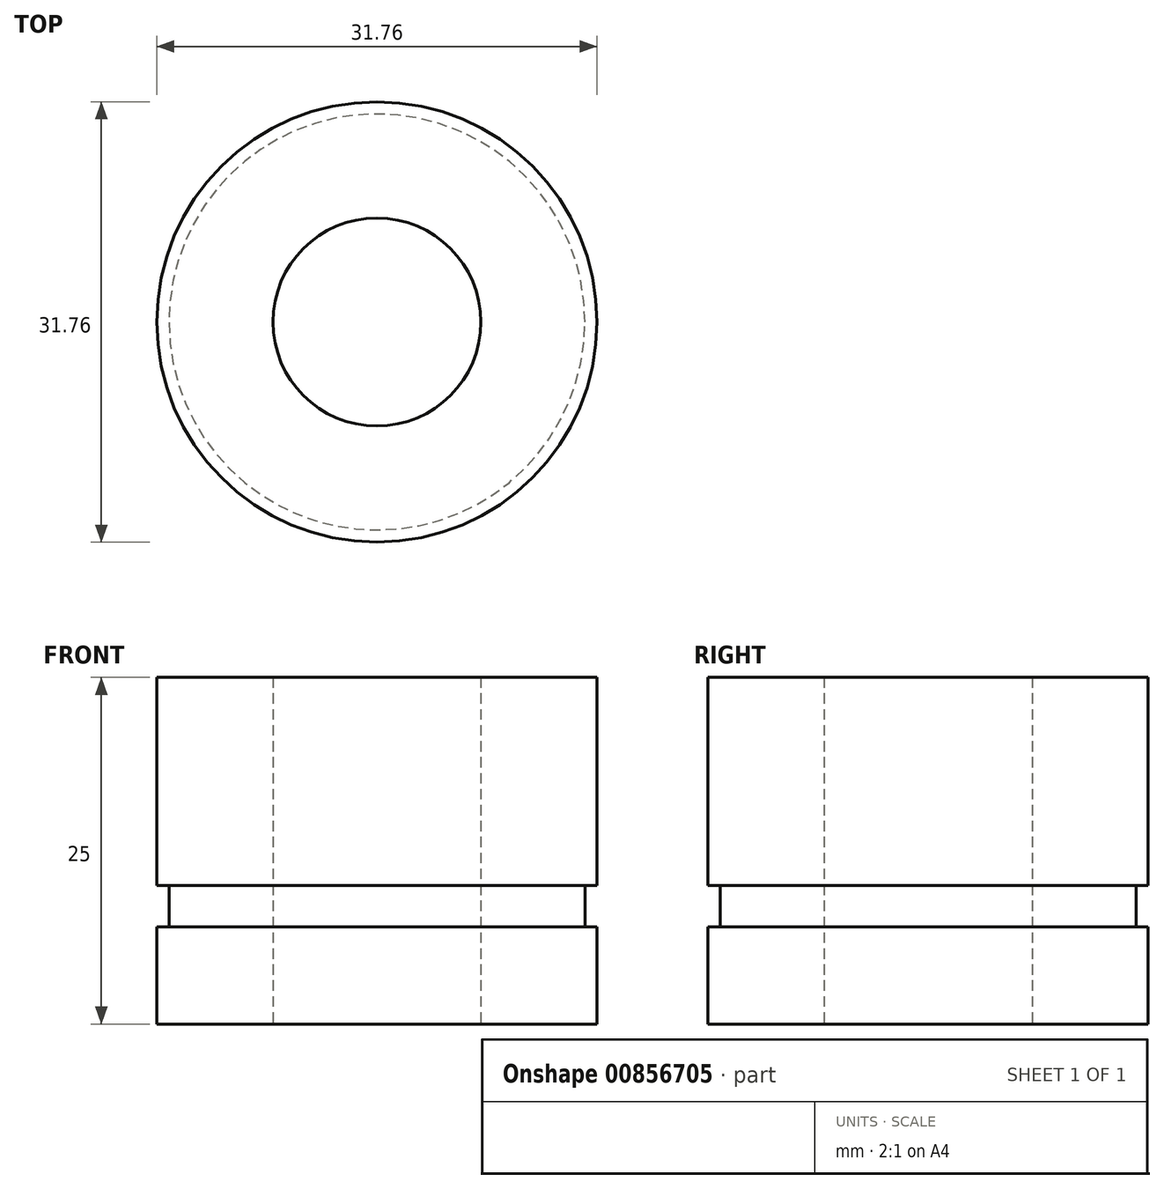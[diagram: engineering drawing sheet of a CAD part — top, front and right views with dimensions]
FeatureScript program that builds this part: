
annotation { "Feature Type Name" : "Feature", "Feature Type Description" : "" }
export const myFeature = defineFeature(function(context is Context, id is Id, definition is map)
    precondition{}
    {
        {
            var Q0;
            Q0=qCreatedBy(makeId("Top.planeOp"),FACE);
            var sketch = newSketch(context, id + "F0", { "sketchPlane" : qUnion([Q0])});
            skCircle(sketch, "E0", {"center": v(0, 0) * mm, "radius": 15.88 * mm});
            skCircle(sketch, "E1", {"center": v(0, 0) * mm, "radius": 7.5 * mm});
            skSolve(sketch);
        }
        {
            var Q0;
            Q0 = qSketchRegion(id + "F0", true);
            extrude(context, id + "F1", {"entities" : qUnion([Q0]), "depth" : 25 * mm, "offsetDistance" : 25 * mm});
        }
        {
            var Q0;
            Q0=qCreatedBy(makeId("Top.planeOp"),FACE);
            cPlane(context, id + "F2", {"entities" : qUnion([Q0]), "cplaneType" : CPlaneType.OFFSET, "offset" : 7 * mm, "width" : 150 * mm, "height" : 150 * mm});
        }
        {
            var Q0;
            Q0=qCreatedBy(id+"F2.planeOp",FACE);
            var sketch = newSketch(context, id + "F3", { "sketchPlane" : qUnion([Q0])});
            skCircle(sketch, "E2", {"center": v(0, 0) * mm, "radius": 15 * mm});
            skCircle(sketch, "E3", {"center": v(0, 0) * mm, "radius": 15.88 * mm});
            skSolve(sketch);
        }
        {
            var Q0;
            Q0 = qSketchRegion(id + "F3", true);
            extrude(context, id + "F4", {"entities" : qUnion([Q0]), "operationType" : NewBodyOperationType.REMOVE, "depth" : 3 * mm, "offsetDistance" : 25 * mm});
        }
    });
